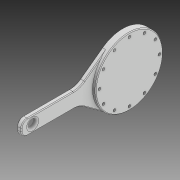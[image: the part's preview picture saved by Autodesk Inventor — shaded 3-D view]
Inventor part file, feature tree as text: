
AUTODESK INVENTOR PART (.ipt)
format: ipt  version: 2020 (Build 240168000, 168)  size: 197,120 bytes
history: native  units: mm
features: extrude x2, fillet x2, sketch x2, chamfer x1
ambient origin geometry x8: Origin, YZ Plane, XZ Plane, XY Plane, X Axis, Y Axis, Z Axis, Center Point
bodies: Solid1 (feature_tree)
feature tree (7):
  extrude  "Extrusion1"  Depth=45.0mm
  extrude  "Extrusion2"  Depth=3.0mm
  fillet  "Fillet1"  Radius=120.0mm
  fillet  "Fillet2"  Radius=20.0mm
  chamfer  "Chamfer1"  Distance=10.0mm
  sketch  "Sketch1"  dims[d0=45.0mm d1=125.0mm]
  sketch  "Sketch2"  dims[d2=3.5mm d3=80.0mm d4=120.0mm d6=360.0deg d8=20.0mm d9=10.0mm d10=15.0mm d11=8.0mm d12=10.0mm d13=0.0mm d14=4.0mm d15=0.0mm d16=185.0mm d17=25.0mm d18=3.0mm d19=1.0mm d20=2.0mm d21=45.0deg]
